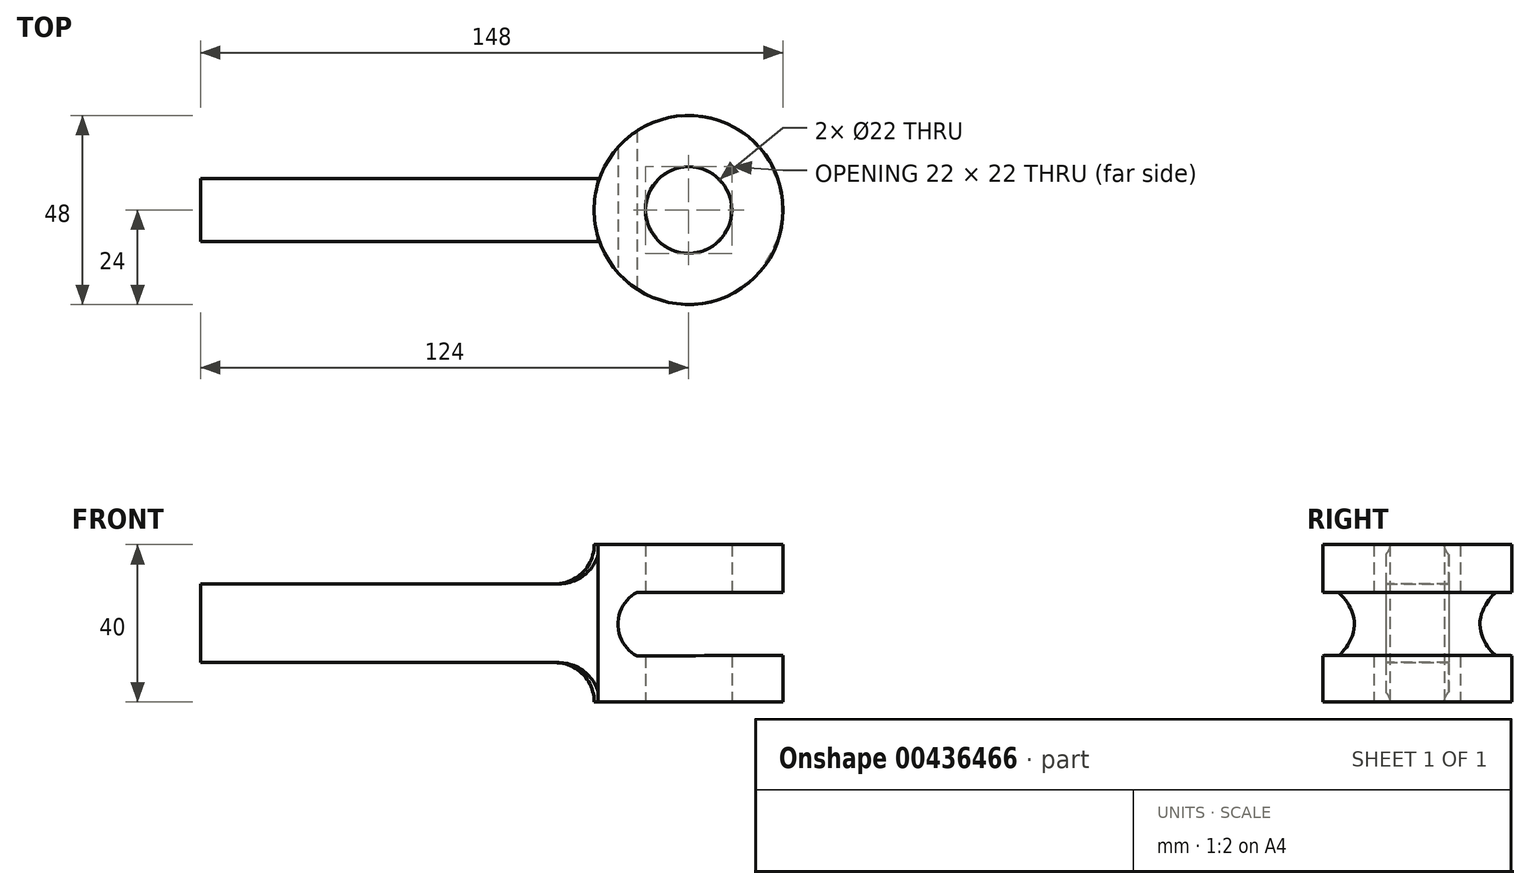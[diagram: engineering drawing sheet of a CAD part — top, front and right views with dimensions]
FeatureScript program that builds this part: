
annotation { "Feature Type Name" : "Feature", "Feature Type Description" : "" }
export const myFeature = defineFeature(function(context is Context, id is Id, definition is map)
    precondition{}
    {
        {
            var Q0;
            Q0=qCreatedBy(makeId("Top.planeOp"),FACE);
            var sketch = newSketch(context, id + "F0", { "sketchPlane" : qUnion([Q0])});
            skCircle(sketch, "E0", {"center": v(0, 0) * mm, "radius": 24 * mm});
            skCircle(sketch, "E1", {"center": v(0, 0) * mm, "radius": 11 * mm});
            skLineSegment(sketch, "E2", {"start": v(24, 0) * mm, "end": v(-24, 0) * mm});
            skSolve(sketch);
        }
        {
            var Q0;
            Q0 = qSketchRegion(id + "F0", true);
            extrude(context, id + "F1", {"entities" : qUnion([Q0]), "depth" : 20 * mm, "hasSecondDirection" : true, "secondDirectionOppositeDirection" : true, "secondDirectionDepth" : 20 * mm});
        }
        {
            var Q0;
            Q0=qCreatedBy(makeId("Top.planeOp"),FACE);
            var sketch = newSketch(context, id + "F2", { "sketchPlane" : qUnion([Q0])});
            skLineSegment(sketch, "E3", {"start": v(16.07, 0) * mm, "end": v(-13.8, 0) * mm});
            skLineSegment(sketch, "E4", {"start": v(-124, 0) * mm, "end": v(-124, 8) * mm});
            skLineSegment(sketch, "E5", {"start": v(-124, 0) * mm, "end": v(-124, -8) * mm});
            skLineSegment(sketch, "E6", {"start": v(-124, -8) * mm, "end": v(-22.98, -8) * mm});
            skLineSegment(sketch, "E7", {"start": v(-124, 8) * mm, "end": v(-22.98, 8) * mm});
            skLineSegment(sketch, "E8", {"start": v(-22.98, 8) * mm, "end": v(-22.98, -8) * mm});
            skSolve(sketch);
        }
        {
            var Q0;
            Q0=makeQuery(id+"F2.imprint","IMPRINT",FACE,{"disambiguationData":[TD([[makeQuery(id+"F2.imprint","IMPRINT",EDGE,{"derivedFrom":sQuery(id+"F2.wireOp",EDGE,"E4")}),-1.0]])]});
            extrude(context, id + "F3", {"entities" : qUnion([Q0]), "operationType" : NewBodyOperationType.ADD, "depth" : 10 * mm, "hasSecondDirection" : true, "secondDirectionOppositeDirection" : true, "secondDirectionDepth" : 10 * mm});
        }
        {
            var Q0;
            Q0=qCreatedBy(makeId("Front.planeOp"),FACE);
            var sketch = newSketch(context, id + "F4", { "sketchPlane" : qUnion([Q0])});
            skPoint(sketch, "E9", {"position": v(24.04, 19.88) * mm});
            skPoint(sketch, "E10", {"position": v(24.13, -20.12) * mm});
            skLineSegment(sketch, "E11", {"start": v(24.04, 19.88) * mm, "end": v(24.04, 7.88) * mm});
            skLineSegment(sketch, "E12", {"start": v(24.13, -20.12) * mm, "end": v(24.13, -8.12) * mm});
            skLineSegment(sketch, "E13", {"start": v(24.13, -8.12) * mm, "end": v(24.04, 7.88) * mm});
            skLineSegment(sketch, "E14", {"start": v(24.04, 7.88) * mm, "end": v(-13.16, 7.88) * mm});
            skLineSegment(sketch, "E15", {"start": v(24.13, -8.12) * mm, "end": v(-13.16, -8.32) * mm});
            skArc(sketch, "E16", {"start": v(-13.16, 7.88) * mm, "mid": v(-17.94, -0.22) * mm, "end": v(-13.16, -8.32) * mm});
            skPoint(sketch, "E17.start.orphan", {"position": v(24.08, 0) * mm});
            skSolve(sketch);
        }
        {
            var Q0;
            Q0 = qSketchRegion(id + "F4", true);
            extrude(context, id + "F5", {"entities" : qUnion([Q0]), "operationType" : NewBodyOperationType.REMOVE, "oppositeDirection" : true, "depth" : 25 * mm, "hasSecondDirection" : true, "secondDirectionOppositeDirection" : false, "secondDirectionDepth" : 25 * mm});
        }
        {
            var Q0;
            Q0=makeQuery(id+"F3.boolean.opBoolean","INTERSECT",EDGE,{"derivedFrom":[makeQuery(id+"F1.opExtrude","SWEPT_FACE",FACE,{"disambiguationData":[OSD([sQuery(id+"F0.wireOp",EDGE,"E0")])]}),makeQuery(id+"F3.opExtrude","CAP_FACE",FACE,{"disambiguationData":[OSD([sQuery(id+"F2.wireOp",EDGE,"E4"),sQuery(id+"F2.wireOp",EDGE,"E5"),sQuery(id+"F2.wireOp",EDGE,"E6"),sQuery(id+"F2.wireOp",EDGE,"E7"),sQuery(id+"F2.wireOp",EDGE,"E8")])],"isStart":false})]});
            fillet(context, id + "F6", {"entities" : qUnion([Q0]), "radius" : 10 * mm, "tangentPropagation" : true, "allowEdgeOverflow" : false});
        }
        {
            var Q0;
            Q0=makeQuery(id+"F3.boolean.opBoolean","INTERSECT",EDGE,{"derivedFrom":[makeQuery(id+"F1.opExtrude","SWEPT_FACE",FACE,{"disambiguationData":[OSD([sQuery(id+"F0.wireOp",EDGE,"E0")])]}),makeQuery(id+"F3.opExtrude","CAP_FACE",FACE,{"disambiguationData":[OSD([sQuery(id+"F2.wireOp",EDGE,"E4"),sQuery(id+"F2.wireOp",EDGE,"E5"),sQuery(id+"F2.wireOp",EDGE,"E6"),sQuery(id+"F2.wireOp",EDGE,"E7"),sQuery(id+"F2.wireOp",EDGE,"E8")])],"isStart":true})]});
            fillet(context, id + "F7", {"entities" : qUnion([Q0]), "radius" : 10 * mm, "tangentPropagation" : true, "allowEdgeOverflow" : false});
        }
    });
